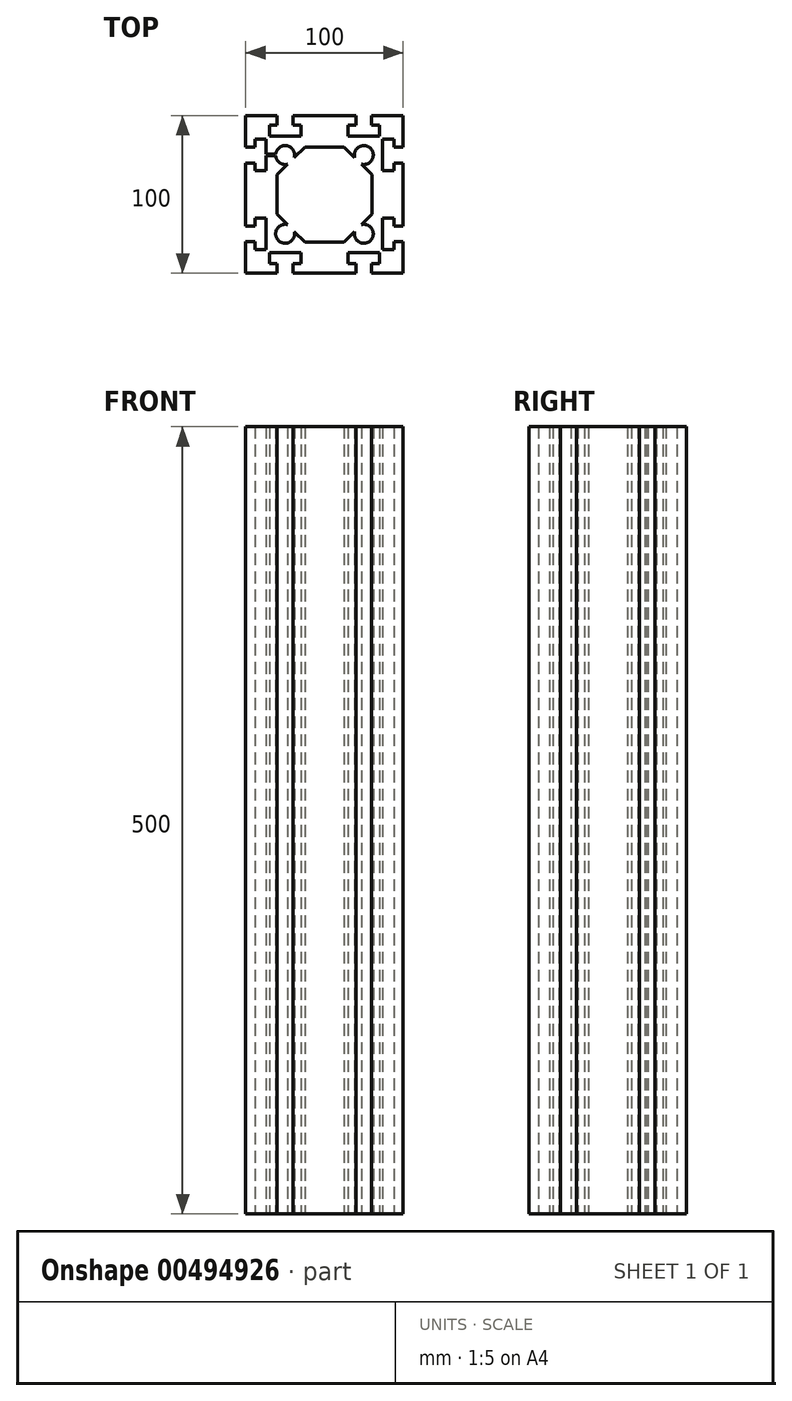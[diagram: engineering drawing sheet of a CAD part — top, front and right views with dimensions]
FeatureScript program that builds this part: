
annotation { "Feature Type Name" : "Feature", "Feature Type Description" : "" }
export const myFeature = defineFeature(function(context is Context, id is Id, definition is map)
    precondition{}
    {
        {
            var Q0;
            Q0=qCreatedBy(makeId("Top.planeOp"),FACE);
            var sketch = newSketch(context, id + "F0", { "sketchPlane" : qUnion([Q0])});
            skLineSegment(sketch, "E0.bottom", {"start": v(-50, 50) * mm, "end": v(-30, 50) * mm});
            skLineSegment(sketch, "E0.left", {"start": v(-50, 50) * mm, "end": v(-50, 30) * mm});
            skArc(sketch, "E1", {"start": v(-19.2, 23.48) * mm, "mid": v(-20.4, 28.86) * mm, "end": v(-25.5, 30.98) * mm});
            skArc(sketch, "E2", {"start": v(23.48, 19.2) * mm, "mid": v(29.24, 29.24) * mm, "end": v(19.2, 23.48) * mm});
            skArc(sketch, "E3", {"start": v(19.2, -23.48) * mm, "mid": v(29.24, -29.24) * mm, "end": v(23.48, -19.2) * mm});
            skArc(sketch, "E4", {"start": v(-23.48, -19.2) * mm, "mid": v(-29.24, -29.24) * mm, "end": v(-19.2, -23.48) * mm});
            skLineSegment(sketch, "E5.bottom", {"start": v(-44, 35) * mm, "end": v(-37, 35) * mm});
            skLineSegment(sketch, "E5.top", {"start": v(-44, 15) * mm, "end": v(-37, 15) * mm});
            skLineSegment(sketch, "E5.left", {"start": v(-44, 35) * mm, "end": v(-44, 30) * mm});
            skLineSegment(sketch, "E5.right", {"start": v(-37, 35) * mm, "end": v(-37, 25.5) * mm});
            skLineSegment(sketch, "E6", {"start": v(-44, 30) * mm, "end": v(-50, 30) * mm});
            skLineSegment(sketch, "E7", {"start": v(-44, 20) * mm, "end": v(-50, 20) * mm});
            skLineSegment(sketch, "E8.trimOffspring", {"start": v(-44, 20) * mm, "end": v(-44, 15) * mm});
            skLineSegment(sketch, "E9.1.0.0", {"start": v(-44, -35) * mm, "end": v(-37, -35) * mm});
            skLineSegment(sketch, "E9.1.0.1", {"start": v(-44, -15) * mm, "end": v(-37, -15) * mm});
            skLineSegment(sketch, "E9.1.0.2", {"start": v(-37, -15) * mm, "end": v(-37, -35) * mm});
            skLineSegment(sketch, "E9.1.0.3", {"start": v(-44, -15) * mm, "end": v(-44, -20) * mm});
            skLineSegment(sketch, "E9.1.0.4", {"start": v(-44, -20) * mm, "end": v(-50, -20) * mm});
            skLineSegment(sketch, "E9.1.0.5", {"start": v(-44, -30) * mm, "end": v(-44, -35) * mm});
            skLineSegment(sketch, "E9.1.0.6", {"start": v(-44, -30) * mm, "end": v(-50, -30) * mm});
            skLineSegment(sketch, "E10", {"start": v(-50, 20) * mm, "end": v(-50, -20) * mm});
            skLineSegment(sketch, "E11", {"start": v(-50, -30) * mm, "end": v(-50, -50) * mm});
            skLineSegment(sketch, "E12.bottom", {"start": v(-35, 44) * mm, "end": v(-30, 44) * mm});
            skLineSegment(sketch, "E12.top", {"start": v(-35, 37) * mm, "end": v(-25.5, 37) * mm});
            skLineSegment(sketch, "E12.left", {"start": v(-35, 44) * mm, "end": v(-35, 37) * mm});
            skLineSegment(sketch, "E12.right", {"start": v(-15, 44) * mm, "end": v(-15, 37) * mm});
            skLineSegment(sketch, "E13.left", {"start": v(-30, 50) * mm, "end": v(-30, 44) * mm});
            skLineSegment(sketch, "E13.right", {"start": v(-20, 50) * mm, "end": v(-20, 44) * mm});
            skLineSegment(sketch, "E14.trimOffspring", {"start": v(-20, 44) * mm, "end": v(-15, 44) * mm});
            skLineSegment(sketch, "E15.trimOffspring", {"start": v(-20, 50) * mm, "end": v(20, 50) * mm});
            skLineSegment(sketch, "E16.1.0.0", {"start": v(15, 44) * mm, "end": v(15, 37) * mm});
            skLineSegment(sketch, "E16.1.0.1", {"start": v(15, 44) * mm, "end": v(20, 44) * mm});
            skLineSegment(sketch, "E16.1.0.2", {"start": v(20, 50) * mm, "end": v(20, 44) * mm});
            skLineSegment(sketch, "E16.1.0.3", {"start": v(30, 44) * mm, "end": v(35, 44) * mm});
            skLineSegment(sketch, "E16.1.0.4", {"start": v(30, 50) * mm, "end": v(30, 44) * mm});
            skLineSegment(sketch, "E16.1.0.5", {"start": v(35, 44) * mm, "end": v(35, 37) * mm});
            skLineSegment(sketch, "E16.1.0.6", {"start": v(15, 37) * mm, "end": v(35, 37) * mm});
            skLineSegment(sketch, "E17.trimOffspring", {"start": v(30, 50) * mm, "end": v(50, 50) * mm});
            skLineSegment(sketch, "E18.MirrorCS", {"start": v(44, -30) * mm, "end": v(44, -35) * mm});
            skLineSegment(sketch, "E19.MirrorCS", {"start": v(44, -15) * mm, "end": v(44, -20) * mm});
            skLineSegment(sketch, "E20.MirrorCS", {"start": v(44, 30) * mm, "end": v(50, 30) * mm});
            skLineSegment(sketch, "E21.MirrorCS", {"start": v(44, 20) * mm, "end": v(50, 20) * mm});
            skLineSegment(sketch, "E22.MirrorCS", {"start": v(44, -30) * mm, "end": v(50, -30) * mm});
            skLineSegment(sketch, "E23.MirrorCS", {"start": v(44, -20) * mm, "end": v(50, -20) * mm});
            skLineSegment(sketch, "E24.MirrorCS", {"start": v(44, 35) * mm, "end": v(37, 35) * mm});
            skLineSegment(sketch, "E25.MirrorCS", {"start": v(44, 35) * mm, "end": v(44, 30) * mm});
            skLineSegment(sketch, "E26.MirrorCS", {"start": v(44, 20) * mm, "end": v(44, 15) * mm});
            skLineSegment(sketch, "E27.MirrorCS", {"start": v(37, 35) * mm, "end": v(37, 15) * mm});
            skLineSegment(sketch, "E28.MirrorCS", {"start": v(44, 15) * mm, "end": v(37, 15) * mm});
            skLineSegment(sketch, "E29.MirrorCS", {"start": v(37, -15) * mm, "end": v(37, -35) * mm});
            skLineSegment(sketch, "E30.MirrorCS", {"start": v(44, -15) * mm, "end": v(37, -15) * mm});
            skLineSegment(sketch, "E31.MirrorCS", {"start": v(44, -35) * mm, "end": v(37, -35) * mm});
            skLineSegment(sketch, "E32", {"start": v(50, 50) * mm, "end": v(50, 30) * mm});
            skLineSegment(sketch, "E33", {"start": v(50, 20) * mm, "end": v(50, -20) * mm});
            skLineSegment(sketch, "E34", {"start": v(50, -30) * mm, "end": v(50, -50) * mm});
            skLineSegment(sketch, "E35.MirrorCS", {"start": v(-35, -44) * mm, "end": v(-35, -37) * mm});
            skLineSegment(sketch, "E36.MirrorCS", {"start": v(-20, -50) * mm, "end": v(-20, -44) * mm});
            skLineSegment(sketch, "E37.MirrorCS", {"start": v(-30, -50) * mm, "end": v(-30, -44) * mm});
            skLineSegment(sketch, "E38.MirrorCS", {"start": v(30, -44) * mm, "end": v(35, -44) * mm});
            skLineSegment(sketch, "E39.MirrorCS", {"start": v(20, -50) * mm, "end": v(20, -44) * mm});
            skLineSegment(sketch, "E40.MirrorCS", {"start": v(35, -44) * mm, "end": v(35, -37) * mm});
            skLineSegment(sketch, "E41.MirrorCS", {"start": v(15, -44) * mm, "end": v(15, -37) * mm});
            skLineSegment(sketch, "E42.MirrorCS", {"start": v(15, -44) * mm, "end": v(20, -44) * mm});
            skLineSegment(sketch, "E43.MirrorCS", {"start": v(-20, -44) * mm, "end": v(-15, -44) * mm});
            skLineSegment(sketch, "E44.MirrorCS", {"start": v(30, -50) * mm, "end": v(30, -44) * mm});
            skLineSegment(sketch, "E45.MirrorCS", {"start": v(-15, -44) * mm, "end": v(-15, -37) * mm});
            skLineSegment(sketch, "E46.MirrorCS", {"start": v(-35, -44) * mm, "end": v(-30, -44) * mm});
            skLineSegment(sketch, "E47.MirrorCS", {"start": v(-50, -50) * mm, "end": v(-30, -50) * mm});
            skLineSegment(sketch, "E48.MirrorCS", {"start": v(30, -50) * mm, "end": v(50, -50) * mm});
            skLineSegment(sketch, "E49.MirrorCS", {"start": v(-35, -37) * mm, "end": v(-15, -37) * mm});
            skLineSegment(sketch, "E50.MirrorCS", {"start": v(-20, -50) * mm, "end": v(20, -50) * mm});
            skLineSegment(sketch, "E51.MirrorCS", {"start": v(15, -37) * mm, "end": v(35, -37) * mm});
            skLineSegment(sketch, "E52", {"start": v(12.5, 30.18) * mm, "end": v(19.2, 23.48) * mm});
            skLineSegment(sketch, "E53", {"start": v(30.18, 12.5) * mm, "end": v(30.18, -12.5) * mm});
            skLineSegment(sketch, "E54", {"start": v(30.18, -12.5) * mm, "end": v(23.48, -19.2) * mm});
            skLineSegment(sketch, "E55", {"start": v(12.5, -30.18) * mm, "end": v(-12.5, -30.18) * mm});
            skLineSegment(sketch, "E56", {"start": v(-12.5, -30.18) * mm, "end": v(-19.2, -23.48) * mm});
            skLineSegment(sketch, "E57", {"start": v(-30.18, -12.5) * mm, "end": v(-30.18, 12.5) * mm});
            skLineSegment(sketch, "E58", {"start": v(-30.18, 12.5) * mm, "end": v(-23.48, 19.2) * mm});
            skLineSegment(sketch, "E59", {"start": v(-12.5, 30.18) * mm, "end": v(12.5, 30.18) * mm});
            skLineSegment(sketch, "E60", {"start": v(0, 0) * mm, "end": v(-30.18, 0) * mm, "construction": true});
            skLineSegment(sketch, "E61", {"start": v(0, 0) * mm, "end": v(30.18, 0) * mm, "construction": true});
            skLineSegment(sketch, "E62", {"start": v(0, 0) * mm, "end": v(0, 30.18) * mm, "construction": true});
            skLineSegment(sketch, "E63", {"start": v(0, 0) * mm, "end": v(0, -30.18) * mm, "construction": true});
            skLineSegment(sketch, "E64.trimOffspring", {"start": v(-23.48, -19.2) * mm, "end": v(-30.18, -12.5) * mm});
            skLineSegment(sketch, "E65.trimOffspring", {"start": v(19.2, -23.48) * mm, "end": v(12.5, -30.18) * mm});
            skLineSegment(sketch, "E66.trimOffspring", {"start": v(23.48, 19.2) * mm, "end": v(30.18, 12.5) * mm});
            skLineSegment(sketch, "E67.trimOffspring", {"start": v(-19.2, 23.48) * mm, "end": v(-12.5, 30.18) * mm});
            skLineSegment(sketch, "E68", {"start": v(-37, 25.5) * mm, "end": v(-30.98, 25.5) * mm});
            skLineSegment(sketch, "E69", {"start": v(-30.98, 24.5) * mm, "end": v(-37, 24.5) * mm});
            skPoint(sketch, "E69.endSnap0", {"position": v(-37, 25) * mm});
            skArc(sketch, "E70.trimOffspring", {"start": v(-30.98, 24.5) * mm, "mid": v(-28.47, 20.1) * mm, "end": v(-23.48, 19.2) * mm});
            skLineSegment(sketch, "E71.trimOffspring", {"start": v(-37, 24.5) * mm, "end": v(-37, 15) * mm});
            skArc(sketch, "E72.trimOffspring", {"start": v(-25.5, 30.98) * mm, "mid": v(-29.24, 29.24) * mm, "end": v(-30.98, 25.5) * mm});
            skLineSegment(sketch, "E73.trimOffspring", {"start": v(-25.5, 37) * mm, "end": v(-15, 37) * mm});
            skSolve(sketch);
        }
        {
            var Q0;
            Q0=qSketchRegion(id+"F0",true);
            extrude(context, id + "F1", {"entities" : qUnion([Q0]), "depth" : 500 * mm});
        }
    });
